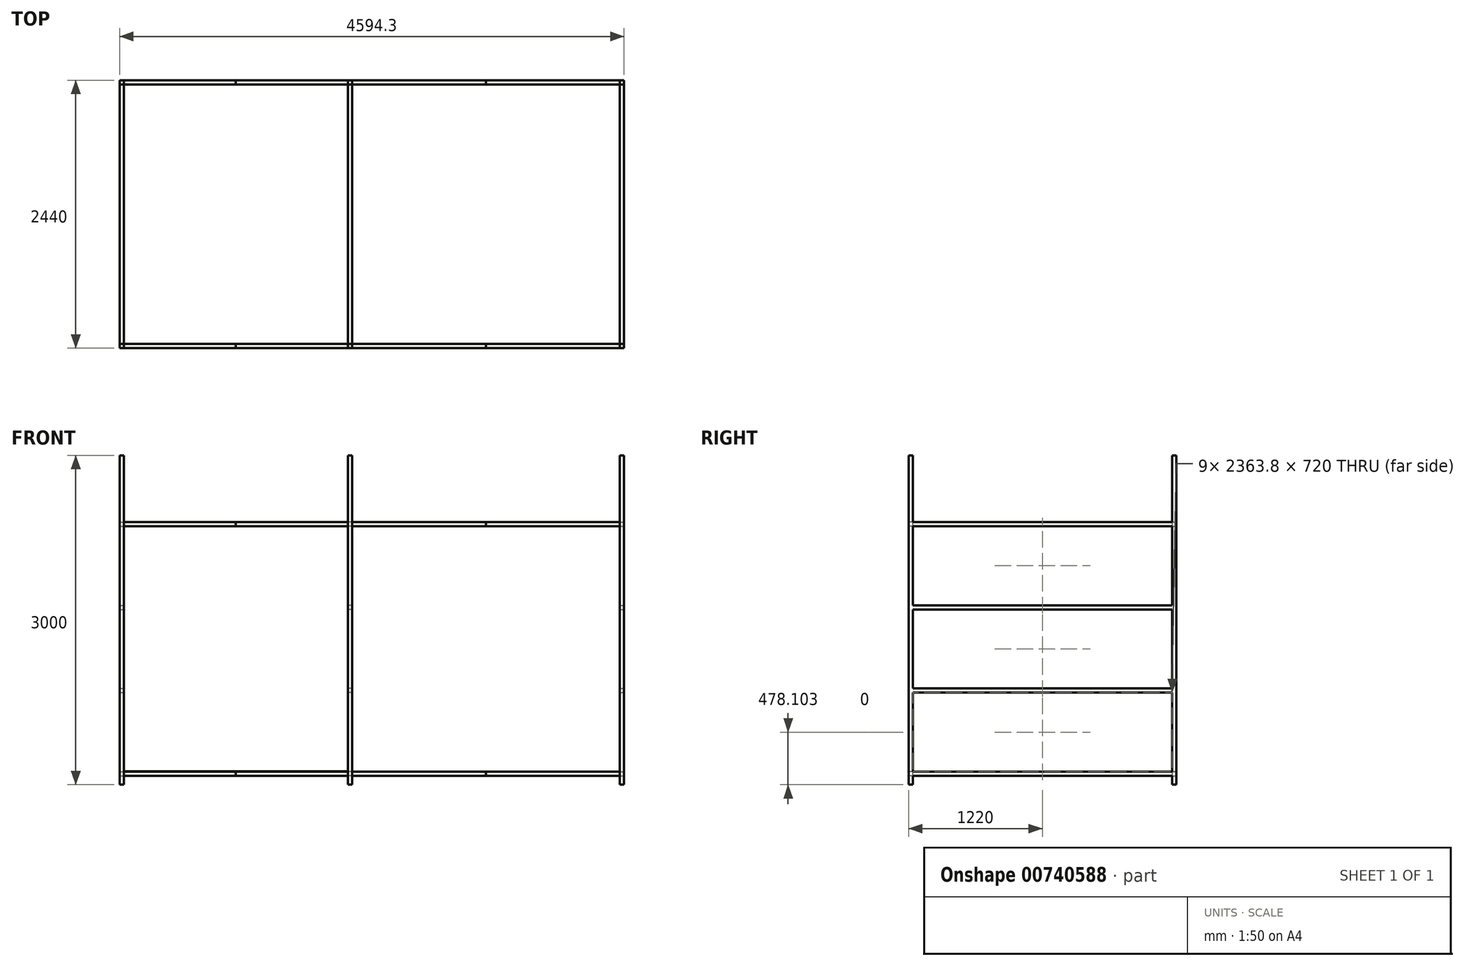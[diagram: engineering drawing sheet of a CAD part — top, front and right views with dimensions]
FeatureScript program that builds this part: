
annotation { "Feature Type Name" : "Feature", "Feature Type Description" : "" }
export const myFeature = defineFeature(function(context is Context, id is Id, definition is map)
    precondition{}
    {
        {
            var Q0;
            Q0=qCreatedBy(makeId("Right.planeOp"),FACE);
            var sketch = newSketch(context, id + "F0", { "sketchPlane" : qUnion([Q0])});
            skLineSegment(sketch, "E0.bottom", {"start": v(-204.95, 1511.6) * mm, "end": v(-166.85, 1511.6) * mm});
            skLineSegment(sketch, "E0.top", {"start": v(-204.95, -1488.4) * mm, "end": v(-166.85, -1488.4) * mm});
            skLineSegment(sketch, "E0.left", {"start": v(-204.95, 1511.6) * mm, "end": v(-204.95, -1488.4) * mm});
            skLineSegment(sketch, "E0.right", {"start": v(-166.85, 1511.6) * mm, "end": v(-166.85, -1488.4) * mm});
            skLineSegment(sketch, "E1.bottom", {"start": v(2196.95, 1511.6) * mm, "end": v(2235.05, 1511.6) * mm});
            skLineSegment(sketch, "E1.top", {"start": v(2196.95, -1488.4) * mm, "end": v(2235.05, -1488.4) * mm});
            skLineSegment(sketch, "E1.left", {"start": v(2196.95, 1511.6) * mm, "end": v(2196.95, -1488.4) * mm});
            skLineSegment(sketch, "E1.right", {"start": v(2235.05, 1511.6) * mm, "end": v(2235.05, -1488.4) * mm});
            skSolve(sketch);
        }
        {
            var Q0;
            Q0 = qSketchRegion(id + "F0", true);
            extrude(context, id + "F1", {"entities" : qUnion([Q0]), "depth" : 38.1 * mm, "offsetDistance" : 25.4 * mm});
        }
        {
            var Q0;
            Q0=makeQuery(id+"F1.opExtrude","SWEPT_FACE",FACE,{"disambiguationData":[OSD([sQuery(id+"F0.wireOp",EDGE,"E0.right")])]});
            var sketch = newSketch(context, id + "F2", { "sketchPlane" : qUnion([Q0])});
            skLineSegment(sketch, "E2.bottom", {"start": v(-38.1, -1408.4) * mm, "end": v(0, -1408.4) * mm});
            skLineSegment(sketch, "E2.top", {"start": v(-38.1, -1370.3) * mm, "end": v(0, -1370.3) * mm});
            skLineSegment(sketch, "E2.left", {"start": v(-38.1, -1408.4) * mm, "end": v(-38.1, -1370.3) * mm});
            skLineSegment(sketch, "E2.right", {"start": v(0, -1408.4) * mm, "end": v(0, -1370.3) * mm});
            skSolve(sketch);
        }
        {
            var Q0;
            Q0 = qSketchRegion(id + "F2", true);
            extrude(context, id + "F3", {"entities" : qUnion([Q0]), "operationType" : NewBodyOperationType.ADD, "depth" : 2363.8 * mm, "offsetDistance" : 25.4 * mm});
        }
        {
            var Q0;
            {var subQ0=sQuery(id+"F0.wireOp",EDGE,"E0.right");var subQ3=sQuery(id+"F0.wireOp",EDGE,"E0.bottom");Q0=makeQuery(id+"F3.boolean.opBoolean","SPLIT",FACE,{"disambiguationData":[TD([makeQuery(id+"F1.opExtrude","SWEPT_FACE",FACE,{"disambiguationData":[OSD([subQ3])]})])],"derivedFrom":makeQuery(id+"F1.opExtrude","SWEPT_FACE",FACE,{"disambiguationData":[OSD([subQ0])]})});}
            var sketch = newSketch(context, id + "F4", { "sketchPlane" : qUnion([Q0])});
            skLineSegment(sketch, "E3.bottom", {"start": v(-38.1, -650.3) * mm, "end": v(0, -650.3) * mm});
            skLineSegment(sketch, "E3.top", {"start": v(-38.1, -612.2) * mm, "end": v(0, -612.2) * mm});
            skLineSegment(sketch, "E3.left", {"start": v(-38.1, -650.3) * mm, "end": v(-38.1, -612.2) * mm});
            skLineSegment(sketch, "E3.right", {"start": v(0, -650.3) * mm, "end": v(0, -612.2) * mm});
            skSolve(sketch);
        }
        {
            var Q0;
            Q0 = qSketchRegion(id + "F4", true);
            extrude(context, id + "F5", {"entities" : qUnion([Q0]), "operationType" : NewBodyOperationType.ADD, "depth" : 2363.8 * mm, "offsetDistance" : 25.4 * mm});
        }
        {
            var Q0;
            {var subQ1=sQuery(id+"F0.wireOp",EDGE,"E0.right");var subQ4=sQuery(id+"F0.wireOp",EDGE,"E0.bottom");var subQ7=makeQuery(id+"F1.opExtrude","SWEPT_FACE",FACE,{"disambiguationData":[OSD([subQ4])]});Q0=makeQuery(id+"F5.boolean.opBoolean","SPLIT",FACE,{"disambiguationData":[TD([subQ7])],"derivedFrom":makeQuery(id+"F3.boolean.opBoolean","SPLIT",FACE,{"disambiguationData":[TD([subQ7])],"derivedFrom":makeQuery(id+"F1.opExtrude","SWEPT_FACE",FACE,{"disambiguationData":[OSD([subQ1])]})})});}
            var sketch = newSketch(context, id + "F6", { "sketchPlane" : qUnion([Q0])});
            skLineSegment(sketch, "E4.bottom", {"start": v(-38.1, 107.8) * mm, "end": v(0, 107.8) * mm});
            skLineSegment(sketch, "E4.top", {"start": v(-38.1, 145.9) * mm, "end": v(0, 145.9) * mm});
            skLineSegment(sketch, "E4.left", {"start": v(-38.1, 107.8) * mm, "end": v(-38.1, 145.9) * mm});
            skLineSegment(sketch, "E4.right", {"start": v(0, 107.8) * mm, "end": v(0, 145.9) * mm});
            skLineSegment(sketch, "E5.bottom", {"start": v(-38.1, 904) * mm, "end": v(0, 904) * mm});
            skLineSegment(sketch, "E5.top", {"start": v(-38.1, 865.9) * mm, "end": v(0, 865.9) * mm});
            skLineSegment(sketch, "E5.left", {"start": v(-38.1, 904) * mm, "end": v(-38.1, 865.9) * mm});
            skLineSegment(sketch, "E5.right", {"start": v(0, 904) * mm, "end": v(0, 865.9) * mm});
            skSolve(sketch);
        }
        {
            var Q0;
            Q0 = qSketchRegion(id + "F6", true);
            extrude(context, id + "F7", {"entities" : qUnion([Q0]), "operationType" : NewBodyOperationType.ADD, "depth" : 2363.8 * mm, "offsetDistance" : 25.4 * mm});
        }
        {
            var Q0;
            Q0=makeQuery(id+"F7.boolean.opBoolean","MERGE",FACE,{"derivedFrom":[makeQuery(id+"F5.boolean.opBoolean","MERGE",FACE,{"derivedFrom":[makeQuery(id+"F3.boolean.opBoolean","MERGE",FACE,{"derivedFrom":[makeQuery(id+"F1.opExtrude","CAP_FACE",FACE,{"disambiguationData":[OSD([sQuery(id+"F0.wireOp",EDGE,"E0.bottom"),sQuery(id+"F0.wireOp",EDGE,"E0.top"),sQuery(id+"F0.wireOp",EDGE,"E0.left"),sQuery(id+"F0.wireOp",EDGE,"E0.right")])],"isStart":true}),makeQuery(id+"F3.opExtrude","SWEPT_FACE",FACE,{"disambiguationData":[OSD([sQuery(id+"F2.wireOp",EDGE,"E2.right")])]})]}),makeQuery(id+"F5.opExtrude","SWEPT_FACE",FACE,{"disambiguationData":[OSD([sQuery(id+"F4.wireOp",EDGE,"E3.right")])]})]}),makeQuery(id+"F7.opExtrude","SWEPT_FACE",FACE,{"disambiguationData":[OSD([sQuery(id+"F6.wireOp",EDGE,"E4.right")])]}),makeQuery(id+"F7.opExtrude","SWEPT_FACE",FACE,{"disambiguationData":[OSD([sQuery(id+"F6.wireOp",EDGE,"E5.right")])]})]});
            var sketch = newSketch(context, id + "F8", { "sketchPlane" : qUnion([Q0])});
            skLineSegment(sketch, "E6.bottom", {"start": v(166.85, 865.9) * mm, "end": v(204.95, 865.9) * mm});
            skLineSegment(sketch, "E6.top", {"start": v(166.85, 904) * mm, "end": v(204.95, 904) * mm});
            skLineSegment(sketch, "E6.left", {"start": v(166.85, 865.9) * mm, "end": v(166.85, 904) * mm});
            skLineSegment(sketch, "E6.right", {"start": v(204.95, 865.9) * mm, "end": v(204.95, 904) * mm});
            skLineSegment(sketch, "E7.bottom", {"start": v(-2196.95, 865.9) * mm, "end": v(-2235.05, 865.9) * mm});
            skLineSegment(sketch, "E7.top", {"start": v(-2196.95, 904) * mm, "end": v(-2235.05, 904) * mm});
            skLineSegment(sketch, "E7.left", {"start": v(-2196.95, 865.9) * mm, "end": v(-2196.95, 904) * mm});
            skLineSegment(sketch, "E7.right", {"start": v(-2235.05, 865.9) * mm, "end": v(-2235.05, 904) * mm});
            skLineSegment(sketch, "E8.bottom", {"start": v(-2196.95, -1408.4) * mm, "end": v(-2235.05, -1408.4) * mm});
            skLineSegment(sketch, "E8.top", {"start": v(-2196.95, -1365.54) * mm, "end": v(-2235.05, -1365.54) * mm});
            skLineSegment(sketch, "E8.left", {"start": v(-2196.95, -1408.4) * mm, "end": v(-2196.95, -1365.54) * mm});
            skLineSegment(sketch, "E8.right", {"start": v(-2235.05, -1408.4) * mm, "end": v(-2235.05, -1365.54) * mm});
            skLineSegment(sketch, "E9.bottom", {"start": v(166.85, -1408.4) * mm, "end": v(204.95, -1408.4) * mm});
            skLineSegment(sketch, "E9.top", {"start": v(166.85, -1370.3) * mm, "end": v(204.95, -1370.3) * mm});
            skLineSegment(sketch, "E9.left", {"start": v(166.85, -1408.4) * mm, "end": v(166.85, -1370.3) * mm});
            skLineSegment(sketch, "E9.right", {"start": v(204.95, -1408.4) * mm, "end": v(204.95, -1370.3) * mm});
            skSolve(sketch);
        }
        {
            var Q0;
            Q0 = qSketchRegion(id + "F8", true);
            extrude(context, id + "F9", {"entities" : qUnion([Q0]), "depth" : 1020 * mm, "offsetDistance" : 25.4 * mm});
        }
        {
            var Q0;
            Q0=makeQuery(id+"F1.opExtrude","SWEPT_BODY",BODY,{"disambiguationData":[OSD([sQuery(id+"F0.wireOp",EDGE,"E0.bottom"),sQuery(id+"F0.wireOp",EDGE,"E0.top"),sQuery(id+"F0.wireOp",EDGE,"E0.left"),sQuery(id+"F0.wireOp",EDGE,"E0.right")])]});
            var Q1;
            Q1=makeQuery(id+"F1.opExtrude","SWEPT_BODY",BODY,{"disambiguationData":[OSD([sQuery(id+"F0.wireOp",EDGE,"E1.bottom"),sQuery(id+"F0.wireOp",EDGE,"E1.top"),sQuery(id+"F0.wireOp",EDGE,"E1.left"),sQuery(id+"F0.wireOp",EDGE,"E1.right")])]});
            var Q2;
            Q2=makeQuery(id+"F9.opExtrude","SWEPT_BODY",BODY,{"disambiguationData":[OSD([sQuery(id+"F8.wireOp",EDGE,"E6.bottom"),sQuery(id+"F8.wireOp",EDGE,"E6.top"),sQuery(id+"F8.wireOp",EDGE,"E6.left"),sQuery(id+"F8.wireOp",EDGE,"E6.right")])]});
            var Q3;
            Q3=makeQuery(id+"F9.opExtrude","SWEPT_BODY",BODY,{"disambiguationData":[OSD([sQuery(id+"F8.wireOp",EDGE,"E7.bottom"),sQuery(id+"F8.wireOp",EDGE,"E7.top"),sQuery(id+"F8.wireOp",EDGE,"E7.left"),sQuery(id+"F8.wireOp",EDGE,"E7.right")])]});
            var Q4;
            Q4=makeQuery(id+"F9.opExtrude","SWEPT_BODY",BODY,{"disambiguationData":[OSD([sQuery(id+"F8.wireOp",EDGE,"E8.bottom"),sQuery(id+"F8.wireOp",EDGE,"E8.top"),sQuery(id+"F8.wireOp",EDGE,"E8.left"),sQuery(id+"F8.wireOp",EDGE,"E8.right")])]});
            var Q5;
            Q5=makeQuery(id+"F9.opExtrude","SWEPT_BODY",BODY,{"disambiguationData":[OSD([sQuery(id+"F8.wireOp",EDGE,"E9.bottom"),sQuery(id+"F8.wireOp",EDGE,"E9.top"),sQuery(id+"F8.wireOp",EDGE,"E9.left"),sQuery(id+"F8.wireOp",EDGE,"E9.right")])]});
            var Q6;
            Q6=makeQuery(id+"F9.opExtrude","CAP_FACE",FACE,{"disambiguationData":[OSD([sQuery(id+"F8.wireOp",EDGE,"E7.bottom"),sQuery(id+"F8.wireOp",EDGE,"E7.top"),sQuery(id+"F8.wireOp",EDGE,"E7.left"),sQuery(id+"F8.wireOp",EDGE,"E7.right")])],"isStart":false});
            mirror(context, id + "F10", {"entities" : qUnion([Q0, Q1, Q2, Q3, Q4, Q5]), "mirrorPlane" : qUnion([Q6])});
        }
        {
            var Q0;
            Q0=makeQuery(id+"F7.boolean.opBoolean","MERGE",FACE,{"derivedFrom":[makeQuery(id+"F5.boolean.opBoolean","MERGE",FACE,{"derivedFrom":[makeQuery(id+"F3.boolean.opBoolean","MERGE",FACE,{"derivedFrom":[makeQuery(id+"F1.opExtrude","CAP_FACE",FACE,{"disambiguationData":[OSD([sQuery(id+"F0.wireOp",EDGE,"E0.bottom"),sQuery(id+"F0.wireOp",EDGE,"E0.top"),sQuery(id+"F0.wireOp",EDGE,"E0.left"),sQuery(id+"F0.wireOp",EDGE,"E0.right")])],"isStart":false}),makeQuery(id+"F3.opExtrude","SWEPT_FACE",FACE,{"disambiguationData":[OSD([sQuery(id+"F2.wireOp",EDGE,"E2.left")])]})]}),makeQuery(id+"F5.opExtrude","SWEPT_FACE",FACE,{"disambiguationData":[OSD([sQuery(id+"F4.wireOp",EDGE,"E3.left")])]})]}),makeQuery(id+"F7.opExtrude","SWEPT_FACE",FACE,{"disambiguationData":[OSD([sQuery(id+"F6.wireOp",EDGE,"E4.left")])]}),makeQuery(id+"F7.opExtrude","SWEPT_FACE",FACE,{"disambiguationData":[OSD([sQuery(id+"F6.wireOp",EDGE,"E5.left")])]})]});
            var sketch = newSketch(context, id + "F11", { "sketchPlane" : qUnion([Q0])});
            skLineSegment(sketch, "E10.bottom", {"start": v(-166.85, 865.9) * mm, "end": v(-204.95, 865.9) * mm});
            skLineSegment(sketch, "E10.top", {"start": v(-166.85, 904) * mm, "end": v(-204.95, 904) * mm});
            skLineSegment(sketch, "E10.left", {"start": v(-166.85, 865.9) * mm, "end": v(-166.85, 904) * mm});
            skLineSegment(sketch, "E10.right", {"start": v(-204.95, 865.9) * mm, "end": v(-204.95, 904) * mm});
            skLineSegment(sketch, "E11.bottom", {"start": v(2196.95, 904) * mm, "end": v(2235.05, 904) * mm});
            skLineSegment(sketch, "E11.top", {"start": v(2196.95, 865.9) * mm, "end": v(2235.05, 865.9) * mm});
            skLineSegment(sketch, "E11.left", {"start": v(2196.95, 904) * mm, "end": v(2196.95, 865.9) * mm});
            skLineSegment(sketch, "E11.right", {"start": v(2235.05, 904) * mm, "end": v(2235.05, 865.9) * mm});
            skLineSegment(sketch, "E12.bottom", {"start": v(-166.85, -1408.4) * mm, "end": v(-204.95, -1408.4) * mm});
            skLineSegment(sketch, "E12.top", {"start": v(-166.85, -1370.3) * mm, "end": v(-204.95, -1370.3) * mm});
            skLineSegment(sketch, "E12.left", {"start": v(-166.85, -1408.4) * mm, "end": v(-166.85, -1370.3) * mm});
            skLineSegment(sketch, "E12.right", {"start": v(-204.95, -1408.4) * mm, "end": v(-204.95, -1370.3) * mm});
            skLineSegment(sketch, "E13.bottom", {"start": v(2196.95, -1370.3) * mm, "end": v(2235.05, -1370.3) * mm});
            skLineSegment(sketch, "E13.top", {"start": v(2196.95, -1408.4) * mm, "end": v(2235.05, -1408.4) * mm});
            skLineSegment(sketch, "E13.left", {"start": v(2196.95, -1370.3) * mm, "end": v(2196.95, -1408.4) * mm});
            skLineSegment(sketch, "E13.right", {"start": v(2235.05, -1370.3) * mm, "end": v(2235.05, -1408.4) * mm});
            skSolve(sketch);
        }
        {
            var Q0;
            Q0 = qSketchRegion(id + "F11", true);
            extrude(context, id + "F12", {"entities" : qUnion([Q0]), "depth" : 1220 * mm, "offsetDistance" : 25.4 * mm});
        }
        {
            var Q0;
            Q0=makeQuery(id+"F1.opExtrude","SWEPT_BODY",BODY,{"disambiguationData":[OSD([sQuery(id+"F0.wireOp",EDGE,"E0.bottom"),sQuery(id+"F0.wireOp",EDGE,"E0.top"),sQuery(id+"F0.wireOp",EDGE,"E0.left"),sQuery(id+"F0.wireOp",EDGE,"E0.right")])]});
            var Q1;
            Q1=makeQuery(id+"F1.opExtrude","SWEPT_BODY",BODY,{"disambiguationData":[OSD([sQuery(id+"F0.wireOp",EDGE,"E1.bottom"),sQuery(id+"F0.wireOp",EDGE,"E1.top"),sQuery(id+"F0.wireOp",EDGE,"E1.left"),sQuery(id+"F0.wireOp",EDGE,"E1.right")])]});
            var Q2;
            Q2=makeQuery(id+"F12.opExtrude","SWEPT_BODY",BODY,{"disambiguationData":[OSD([sQuery(id+"F11.wireOp",EDGE,"E13.bottom"),sQuery(id+"F11.wireOp",EDGE,"E13.top"),sQuery(id+"F11.wireOp",EDGE,"E13.left"),sQuery(id+"F11.wireOp",EDGE,"E13.right")])]});
            var Q3;
            Q3=makeQuery(id+"F12.opExtrude","SWEPT_BODY",BODY,{"disambiguationData":[OSD([sQuery(id+"F11.wireOp",EDGE,"E12.bottom"),sQuery(id+"F11.wireOp",EDGE,"E12.top"),sQuery(id+"F11.wireOp",EDGE,"E12.left"),sQuery(id+"F11.wireOp",EDGE,"E12.right")])]});
            var Q4;
            Q4=makeQuery(id+"F12.opExtrude","SWEPT_BODY",BODY,{"disambiguationData":[OSD([sQuery(id+"F11.wireOp",EDGE,"E11.bottom"),sQuery(id+"F11.wireOp",EDGE,"E11.top"),sQuery(id+"F11.wireOp",EDGE,"E11.left"),sQuery(id+"F11.wireOp",EDGE,"E11.right")])]});
            var Q5;
            Q5=makeQuery(id+"F12.opExtrude","SWEPT_BODY",BODY,{"disambiguationData":[OSD([sQuery(id+"F11.wireOp",EDGE,"E10.bottom"),sQuery(id+"F11.wireOp",EDGE,"E10.top"),sQuery(id+"F11.wireOp",EDGE,"E10.left"),sQuery(id+"F11.wireOp",EDGE,"E10.right")])]});
            var Q6;
            Q6=makeQuery(id+"F12.opExtrude","CAP_FACE",FACE,{"disambiguationData":[OSD([sQuery(id+"F11.wireOp",EDGE,"E10.bottom"),sQuery(id+"F11.wireOp",EDGE,"E10.top"),sQuery(id+"F11.wireOp",EDGE,"E10.left"),sQuery(id+"F11.wireOp",EDGE,"E10.right")])],"isStart":false});
            mirror(context, id + "F13", {"entities" : qUnion([Q0, Q1, Q2, Q3, Q4, Q5]), "mirrorPlane" : qUnion([Q6])});
        }
    });
